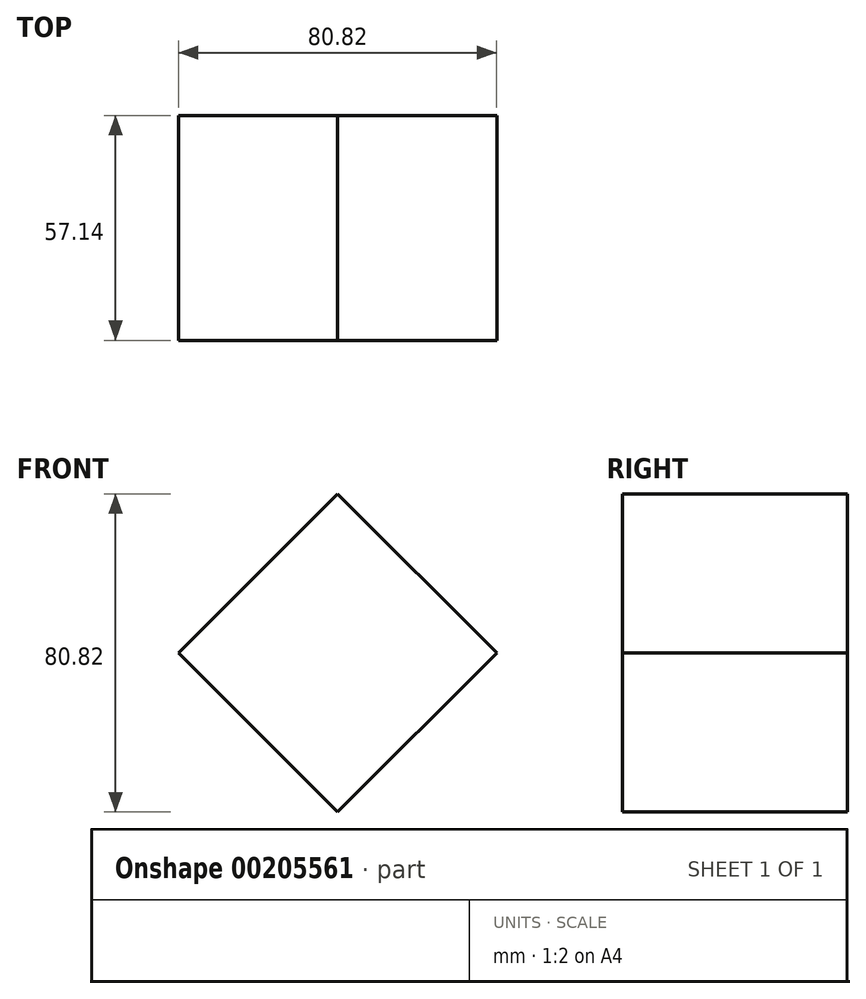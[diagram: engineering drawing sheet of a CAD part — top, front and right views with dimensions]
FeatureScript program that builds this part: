
annotation { "Feature Type Name" : "Feature", "Feature Type Description" : "" }
export const myFeature = defineFeature(function(context is Context, id is Id, definition is map)
    precondition{}
    {
        {
            var Q0;
            Q0=qCreatedBy(makeId("Front.planeOp"),FACE);
            var sketch = newSketch(context, id + "F0", { "sketchPlane" : qUnion([Q0])});
            skLineSegment(sketch, "E0", {"start": v(40.41, 0) * mm, "end": v(0, 40.41) * mm});
            skLineSegment(sketch, "E1", {"start": v(0, 40.41) * mm, "end": v(-40.41, 0) * mm});
            skLineSegment(sketch, "E2", {"start": v(-40.41, 0) * mm, "end": v(0, -40.41) * mm});
            skLineSegment(sketch, "E3", {"start": v(0, -40.41) * mm, "end": v(40.41, 0) * mm});
            skSolve(sketch);
        }
        {
            var Q0;
            Q0=qSketchRegion(id+"F0",true);
            extrude(context, id + "F1", {"entities" : qUnion([Q0]), "depth" : 57.15 * mm, "symmetric" : true});
        }
        {
            var Q0;
            Q0=qCreatedBy(makeId("Front.planeOp"),FACE);
            var sketch = newSketch(context, id + "F2", { "sketchPlane" : qUnion([Q0])});
            skLineSegment(sketch, "E4", {"start": v(0, 0) * mm, "end": v(-105.52, -105.52) * mm, "construction": true});
            skLineSegment(sketch, "E5", {"start": v(0, 0) * mm, "end": v(105.52, -105.52) * mm, "construction": true});
            skSolve(sketch);
        }
    });
